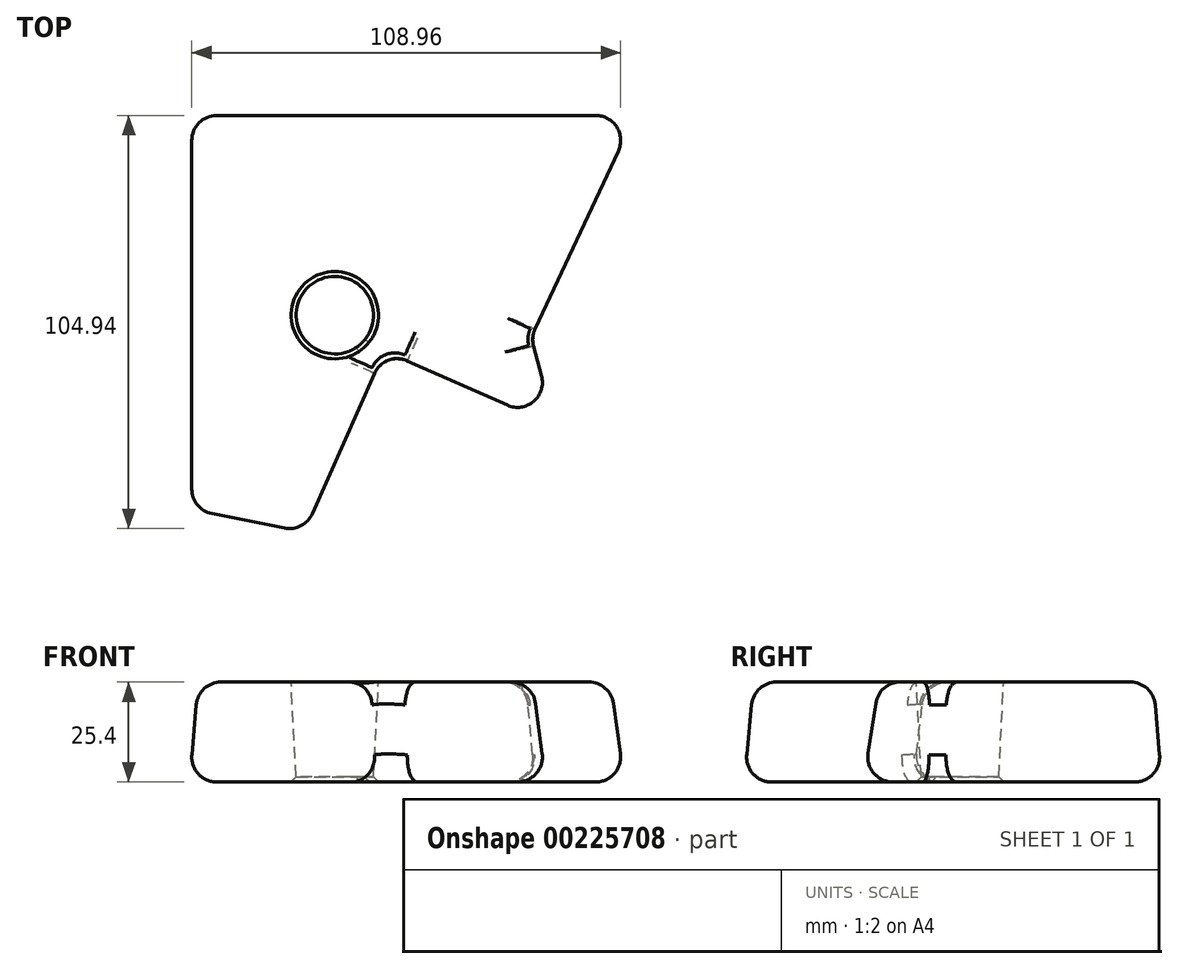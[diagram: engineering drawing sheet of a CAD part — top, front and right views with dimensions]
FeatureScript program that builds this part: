
annotation { "Feature Type Name" : "Feature", "Feature Type Description" : "" }
export const myFeature = defineFeature(function(context is Context, id is Id, definition is map)
    precondition{}
    {
        {
            var Q0;
            Q0=qCreatedBy(makeId("Top.planeOp"),FACE);
            var sketch = newSketch(context, id + "F0", { "sketchPlane" : qUnion([Q0])});
            skLineSegment(sketch, "E0", {"start": v(-60.3, -40.05) * mm, "end": v(-60.3, 61.13) * mm});
            skLineSegment(sketch, "E1", {"start": v(-60.3, 61.13) * mm, "end": v(53.77, 61.13) * mm});
            skLineSegment(sketch, "E2", {"start": v(53.77, 61.13) * mm, "end": v(27.13, 4.12) * mm});
            skLineSegment(sketch, "E3", {"start": v(27.13, 4.12) * mm, "end": v(33.44, -19.46) * mm});
            skLineSegment(sketch, "E4", {"start": v(33.44, -19.46) * mm, "end": v(-10.45, 0) * mm});
            skLineSegment(sketch, "E5", {"start": v(-10.45, 0) * mm, "end": v(-30.8, -45.92) * mm});
            skLineSegment(sketch, "E6", {"start": v(-30.8, -45.92) * mm, "end": v(-60.3, -40.05) * mm});
            skSolve(sketch);
        }
        {
            var Q0;
            Q0 = qSketchRegion(id + "F0", true);
            extrude(context, id + "F1", {"entities" : qUnion([Q0]), "depth" : 25.4 * mm, "hasDraft" : true, "draftAngle" : 5 * degree, "draftPullDirection" : true});
        }
        {
            var Q0;
            Q0=makeQuery(id+"F1.opExtrude","CAP_FACE",FACE,{"disambiguationData":[OSD([sQuery(id+"F0.wireOp",EDGE,"E0"),sQuery(id+"F0.wireOp",EDGE,"E1"),sQuery(id+"F0.wireOp",EDGE,"E2"),sQuery(id+"F0.wireOp",EDGE,"E3"),sQuery(id+"F0.wireOp",EDGE,"E4"),sQuery(id+"F0.wireOp",EDGE,"E5"),sQuery(id+"F0.wireOp",EDGE,"E6")])],"isStart":false});
            var Q1;
            Q1=makeQuery(id+"F1.opExtrude","SWEPT_EDGE",EDGE,{"disambiguationData":[OSD([sQuery(id+"F0.wireOp",EDGE,"E5"),sQuery(id+"F0.wireOp",EDGE,"E6")])]});
            var Q2;
            Q2=makeQuery(id+"F1.opExtrude","SWEPT_EDGE",EDGE,{"disambiguationData":[OSD([sQuery(id+"F0.wireOp",EDGE,"E0"),sQuery(id+"F0.wireOp",EDGE,"E6")])]});
            var Q3;
            Q3=makeQuery(id+"F1.opExtrude","SWEPT_FACE",FACE,{"disambiguationData":[OSD([sQuery(id+"F0.wireOp",EDGE,"E5")])]});
            var Q4;
            Q4=makeQuery(id+"F1.opExtrude","SWEPT_EDGE",EDGE,{"disambiguationData":[OSD([sQuery(id+"F0.wireOp",EDGE,"E3"),sQuery(id+"F0.wireOp",EDGE,"E4")])]});
            var Q5;
            Q5=makeQuery(id+"F1.opExtrude","SWEPT_EDGE",EDGE,{"disambiguationData":[OSD([sQuery(id+"F0.wireOp",EDGE,"E2"),sQuery(id+"F0.wireOp",EDGE,"E3")])]});
            var Q6;
            Q6=makeQuery(id+"F1.opExtrude","SWEPT_EDGE",EDGE,{"disambiguationData":[OSD([sQuery(id+"F0.wireOp",EDGE,"E1"),sQuery(id+"F0.wireOp",EDGE,"E2")])]});
            var Q7;
            Q7=makeQuery(id+"F1.opExtrude","SWEPT_EDGE",EDGE,{"disambiguationData":[OSD([sQuery(id+"F0.wireOp",EDGE,"E0"),sQuery(id+"F0.wireOp",EDGE,"E1")])]});
            var Q8;
            Q8=makeQuery(id+"F1.opExtrude","CAP_EDGE",EDGE,{"disambiguationData":[OSD([sQuery(id+"F0.wireOp",EDGE,"E6")])],"isStart":true});
            var Q9;
            Q9=makeQuery(id+"F1.opExtrude","CAP_EDGE",EDGE,{"disambiguationData":[OSD([sQuery(id+"F0.wireOp",EDGE,"E0")])],"isStart":true});
            var Q10;
            Q10=makeQuery(id+"F1.opExtrude","CAP_EDGE",EDGE,{"disambiguationData":[OSD([sQuery(id+"F0.wireOp",EDGE,"E0")])],"isStart":false});
            var Q11;
            Q11=makeQuery(id+"F1.opExtrude","CAP_EDGE",EDGE,{"disambiguationData":[OSD([sQuery(id+"F0.wireOp",EDGE,"E2")])],"isStart":true});
            var Q12;
            Q12=makeQuery(id+"F1.opExtrude","CAP_EDGE",EDGE,{"disambiguationData":[OSD([sQuery(id+"F0.wireOp",EDGE,"E5")])],"isStart":true});
            var Q13;
            Q13=makeQuery(id+"F1.opExtrude","CAP_EDGE",EDGE,{"disambiguationData":[OSD([sQuery(id+"F0.wireOp",EDGE,"E1")])],"isStart":true});
            var Q14;
            Q14=makeQuery(id+"F1.opExtrude","CAP_EDGE",EDGE,{"disambiguationData":[OSD([sQuery(id+"F0.wireOp",EDGE,"E4")])],"isStart":true});
            var Q15;
            Q15=makeQuery(id+"F1.opExtrude","CAP_EDGE",EDGE,{"disambiguationData":[OSD([sQuery(id+"F0.wireOp",EDGE,"E1")])],"isStart":false});
            var Q16;
            Q16=makeQuery(id+"F1.opExtrude","CAP_EDGE",EDGE,{"disambiguationData":[OSD([sQuery(id+"F0.wireOp",EDGE,"E5")])],"isStart":false});
            var Q17;
            Q17=makeQuery(id+"F1.opExtrude","CAP_EDGE",EDGE,{"disambiguationData":[OSD([sQuery(id+"F0.wireOp",EDGE,"E6")])],"isStart":false});
            var Q18;
            Q18=makeQuery(id+"F1.opExtrude","CAP_EDGE",EDGE,{"disambiguationData":[OSD([sQuery(id+"F0.wireOp",EDGE,"E3")])],"isStart":false});
            var Q19;
            Q19=makeQuery(id+"F1.opExtrude","CAP_EDGE",EDGE,{"disambiguationData":[OSD([sQuery(id+"F0.wireOp",EDGE,"E3")])],"isStart":true});
            var Q20;
            Q20=makeQuery(id+"F1.opExtrude","SWEPT_EDGE",EDGE,{"disambiguationData":[OSD([sQuery(id+"F0.wireOp",EDGE,"E4"),sQuery(id+"F0.wireOp",EDGE,"E5")])]});
            var Q21;
            Q21=makeQuery(id+"F1.opExtrude","CAP_EDGE",EDGE,{"disambiguationData":[OSD([sQuery(id+"F0.wireOp",EDGE,"E4")])],"isStart":false});
            var Q22;
            Q22=makeQuery(id+"F1.opExtrude","CAP_EDGE",EDGE,{"disambiguationData":[OSD([sQuery(id+"F0.wireOp",EDGE,"E2")])],"isStart":false});
            fillet(context, id + "F2", {"entities" : qUnion([Q0, Q1, Q2, Q3, Q4, Q5, Q6, Q7, Q8, Q9, Q10, Q11, Q12, Q13, Q14, Q15, Q16, Q17, Q18, Q19, Q20, Q21, Q22]), "radius" : 6.35 * mm, "tangentPropagation" : true, "allowEdgeOverflow" : false});
        }
        {
            var Q0;
            Q0=makeQuery(id+"F1.opExtrude","CAP_FACE",FACE,{"disambiguationData":[OSD([sQuery(id+"F0.wireOp",EDGE,"E0"),sQuery(id+"F0.wireOp",EDGE,"E1"),sQuery(id+"F0.wireOp",EDGE,"E2"),sQuery(id+"F0.wireOp",EDGE,"E3"),sQuery(id+"F0.wireOp",EDGE,"E4"),sQuery(id+"F0.wireOp",EDGE,"E5"),sQuery(id+"F0.wireOp",EDGE,"E6")])],"isStart":false});
            var sketch = newSketch(context, id + "F3", { "sketchPlane" : qUnion([Q0])});
            skCircle(sketch, "E7", {"center": v(-23.39, 9.82) * mm, "radius": 11.1 * mm});
            skPoint(sketch, "E7.centerSnap0", {"position": v(-52.26, 9.82) * mm});
            skSolve(sketch);
        }
        {
            var Q0;
            Q0 = qSketchRegion(id + "F3", true);
            extrude(context, id + "F4", {"entities" : qUnion([Q0]), "operationType" : NewBodyOperationType.REMOVE, "oppositeDirection" : true, "depth" : 50.8 * mm, "hasDraft" : true, "draftAngle" : 3 * degree, "draftPullDirection" : true});
        }
        {
            var Q0;
            Q0=makeQuery(id+"F4.boolean.opBoolean","COPY",EDGE,{"derivedFrom":makeQuery(id+"F4.opExtrude","CAP_EDGE",EDGE,{"disambiguationData":[OSD([sQuery(id+"F3.wireOp",EDGE,"E7")])],"isStart":true})});
            var Q1;
            Q1=makeQuery(id+"F4.boolean.opBoolean","INTERSECT",EDGE,{"derivedFrom":[makeQuery(id+"F1.opExtrude","CAP_FACE",FACE,{"disambiguationData":[OSD([sQuery(id+"F0.wireOp",EDGE,"E0"),sQuery(id+"F0.wireOp",EDGE,"E1"),sQuery(id+"F0.wireOp",EDGE,"E2"),sQuery(id+"F0.wireOp",EDGE,"E3"),sQuery(id+"F0.wireOp",EDGE,"E4"),sQuery(id+"F0.wireOp",EDGE,"E5"),sQuery(id+"F0.wireOp",EDGE,"E6")])],"isStart":true}),makeQuery(id+"F4.opExtrude","SWEPT_FACE",FACE,{"disambiguationData":[OSD([sQuery(id+"F3.wireOp",EDGE,"E7")])]})]});
            var Q2;
            {var subQ0=sQuery(id+"F0.wireOp",EDGE,"E5");Q2=makeQuery(id+"F4.boolean.opBoolean","INTERSECT",EDGE,{"derivedFrom":[makeQuery(id+"F2.opFillet","BLEND_FACE",FACE,{"disambiguationData":[OSD([subQ0]),TDD([makeQuery(id+"F1.opExtrude","CAP_EDGE",EDGE,{"disambiguationData":[OSD([subQ0])],"isStart":false})])]}),makeQuery(id+"F4.opExtrude","SWEPT_FACE",FACE,{"disambiguationData":[OSD([sQuery(id+"F3.wireOp",EDGE,"E7")])]})]});}
            var Q3;
            Q3=makeQuery(id+"F4.boolean.opBoolean","INTERSECT",EDGE,{"derivedFrom":[makeQuery(id+"F1.opExtrude","SWEPT_FACE",FACE,{"disambiguationData":[OSD([sQuery(id+"F0.wireOp",EDGE,"E5")])]}),makeQuery(id+"F4.opExtrude","SWEPT_FACE",FACE,{"disambiguationData":[OSD([sQuery(id+"F3.wireOp",EDGE,"E7")])]})]});
            var Q4;
            {var subQ0=sQuery(id+"F0.wireOp",EDGE,"E5");Q4=makeQuery(id+"F4.boolean.opBoolean","INTERSECT",EDGE,{"derivedFrom":[makeQuery(id+"F2.opFillet","BLEND_FACE",FACE,{"disambiguationData":[OSD([subQ0]),TDD([makeQuery(id+"F1.opExtrude","CAP_EDGE",EDGE,{"disambiguationData":[OSD([subQ0])],"isStart":true})])]}),makeQuery(id+"F4.opExtrude","SWEPT_FACE",FACE,{"disambiguationData":[OSD([sQuery(id+"F3.wireOp",EDGE,"E7")])]})]});}
            var Q5;
            Q5=makeQuery(id+"F4.boolean.opBoolean","INTERSECT",EDGE,{"derivedFrom":[makeQuery(id+"F1.opExtrude","SWEPT_FACE",FACE,{"disambiguationData":[OSD([sQuery(id+"F0.wireOp",EDGE,"E4")])]}),makeQuery(id+"F4.opExtrude","SWEPT_FACE",FACE,{"disambiguationData":[OSD([sQuery(id+"F3.wireOp",EDGE,"E7")])]})]});
            var Q6;
            {var subQ0=sQuery(id+"F0.wireOp",EDGE,"E4");Q6=makeQuery(id+"F4.boolean.opBoolean","INTERSECT",EDGE,{"derivedFrom":[makeQuery(id+"F2.opFillet","BLEND_FACE",FACE,{"disambiguationData":[OSD([subQ0]),TDD([makeQuery(id+"F1.opExtrude","CAP_EDGE",EDGE,{"disambiguationData":[OSD([subQ0])],"isStart":false})])]}),makeQuery(id+"F4.opExtrude","SWEPT_FACE",FACE,{"disambiguationData":[OSD([sQuery(id+"F3.wireOp",EDGE,"E7")])]})]});}
            var Q7;
            {var subQ0=sQuery(id+"F0.wireOp",EDGE,"E4");Q7=makeQuery(id+"F4.boolean.opBoolean","INTERSECT",EDGE,{"derivedFrom":[makeQuery(id+"F2.opFillet","BLEND_FACE",FACE,{"disambiguationData":[OSD([subQ0]),TDD([makeQuery(id+"F1.opExtrude","CAP_EDGE",EDGE,{"disambiguationData":[OSD([subQ0])],"isStart":true})])]}),makeQuery(id+"F4.opExtrude","SWEPT_FACE",FACE,{"disambiguationData":[OSD([sQuery(id+"F3.wireOp",EDGE,"E7")])]})]});}
            var Q8;
            {var subQ0=sQuery(id+"F0.wireOp",EDGE,"E4");var subQ1=sQuery(id+"F0.wireOp",EDGE,"E3");Q8=makeQuery(id+"F2.opFillet","BLEND_EDGE",EDGE,{"blendedFrom":[makeQuery(id+"F1.opExtrude","CAP_VERTEX",VERTEX,{"disambiguationData":[OSD([subQ1,subQ0])],"isStart":false}),makeQuery(id+"F1.opExtrude","SWEPT_EDGE",EDGE,{"disambiguationData":[OSD([subQ1,subQ0])]})],"blendedInto":[]});}
            var Q9;
            {var subQ0=sQuery(id+"F0.wireOp",EDGE,"E3");Q9=makeQuery(id+"F2.opFillet","BLEND_EDGE",EDGE,{"blendedFrom":[makeQuery(id+"F1.opExtrude","CAP_VERTEX",VERTEX,{"disambiguationData":[OSD([subQ0,sQuery(id+"F0.wireOp",EDGE,"E4")])],"isStart":false}),makeQuery(id+"F1.opExtrude","CAP_EDGE",EDGE,{"disambiguationData":[OSD([subQ0])],"isStart":false})],"blendedInto":[]});}
            var Q10;
            {var subQ0=sQuery(id+"F0.wireOp",EDGE,"E4");Q10=makeQuery(id+"F2.opFillet","BLEND_EDGE",EDGE,{"blendedFrom":[makeQuery(id+"F1.opExtrude","CAP_VERTEX",VERTEX,{"disambiguationData":[OSD([sQuery(id+"F0.wireOp",EDGE,"E3"),subQ0])],"isStart":false}),makeQuery(id+"F1.opExtrude","CAP_EDGE",EDGE,{"disambiguationData":[OSD([subQ0])],"isStart":false})],"blendedInto":[]});}
            chamfer(context, id + "F5", {"entities" : qUnion([Q0, Q1, Q2, Q3, Q4, Q5, Q6, Q7, Q8, Q9, Q10]), "width" : 1.27 * mm, "tangentPropagation" : true});
        }
    });
